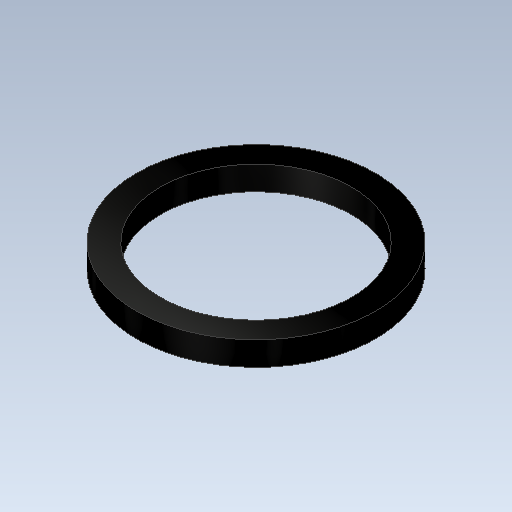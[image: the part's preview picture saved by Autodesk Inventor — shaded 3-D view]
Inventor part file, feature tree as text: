
AUTODESK INVENTOR PART (.ipt)
format: ipt  version: 2020.1 (Build 241239000, 239)  size: 99,328 bytes
history: native  units: mm
features: extrude x1, sketch x1
ambient origin geometry x8: Origin, YZ Plane, XZ Plane, XY Plane, X Axis, Y Axis, Z Axis, Center Point
bodies: Solid1 (feature_tree)
feature tree (2):
  extrude  "Extrusion1"  Depth=10.0mm
  sketch  "Sketch1"  dims[d0=8.0mm d1=10.0mm d2=1.0mm d3=0.0mm]
